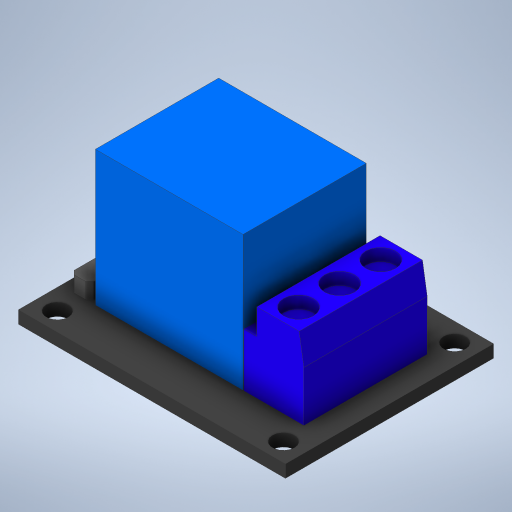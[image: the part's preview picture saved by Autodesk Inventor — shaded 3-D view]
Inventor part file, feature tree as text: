
AUTODESK INVENTOR PART (.ipt)
format: ipt  version: 2023 (Build 270158000, 158)  size: 329,216 bytes
history: native  units: mm
features: extrude x5, sketch x5, other x1, chamfer x1, projected_geometry x1
ambient origin geometry x8: Origin, YZ Plane, XZ Plane, XY Plane, X Axis, Y Axis, Z Axis, Center Point
bodies: Body1 (feature_tree)
feature tree (13):
  other  "솔리드1"
  extrude  "돌출1"  Depth=34.0mm
  extrude  "돌출2"  Depth=26.5mm
  extrude  "돌출3"  Depth=28.8mm
  extrude  "돌출4"  Depth=2.8mm
  extrude  "돌출5"  Depth=21.8mm
  chamfer  "모따기1"  Distance=1.6mm
  sketch  "스케치1"
  sketch  "스케치2"
  sketch  "스케치3"
  sketch  "스케치4"
  projected_geometry  "투영된 루프1"
  sketch  "스케치5"
